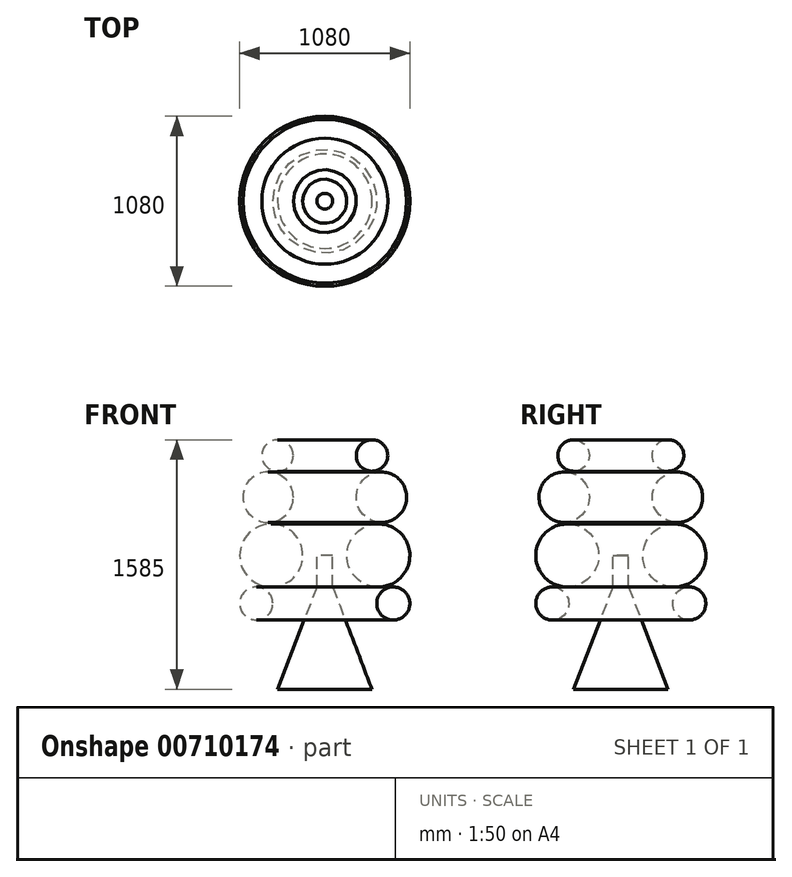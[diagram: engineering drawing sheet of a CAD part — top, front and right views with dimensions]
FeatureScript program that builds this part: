
annotation { "Feature Type Name" : "Feature", "Feature Type Description" : "" }
export const myFeature = defineFeature(function(context is Context, id is Id, definition is map)
    precondition{}
    {
        {
            var Q0;
            Q0=qCreatedBy(makeId("Front.planeOp"),FACE);
            var sketch = newSketch(context, id + "F0", { "sketchPlane" : qUnion([Q0])});
            skCircle(sketch, "E0", {"center": v(-340, 0) * mm, "radius": 200 * mm});
            skLineSegment(sketch, "E1", {"start": v(-340, 0) * mm, "end": v(0, 0) * mm});
            skLineSegment(sketch, "E2", {"start": v(0, 0) * mm, "end": v(0, 197.46) * mm});
            skSolve(sketch);
        }
        {
            var Q0;
            Q0=makeQuery(id+"F0.imprint","IMPRINT",FACE,{"disambiguationData":[TD([[makeQuery(id+"F0.imprint","IMPRINT",EDGE,{"derivedFrom":sQuery(id+"F0.wireOp",EDGE,"E0")}),1.0]])]});
            var Q1;
            Q1=sQuery(id+"F0.wireOp",EDGE,"E2");
            revolve(context, id + "F1", {"surfaceOperationType" : NewSurfaceOperationType.NEW, "entities" : qUnion([Q0]), "axis" : qUnion([Q1]), "revolveType" : RevolveType.FULL});
        }
        {
            var Q0;
            Q0=qCreatedBy(makeId("Front.planeOp"),FACE);
            var sketch = newSketch(context, id + "F2", { "sketchPlane" : qUnion([Q0])});
            skCircle(sketch, "E3", {"center": v(-435, -305) * mm, "radius": 105 * mm});
            skSolve(sketch);
        }
        {
            var Q0;
            Q0=makeQuery(id+"F2.imprint","IMPRINT",FACE,{"disambiguationData":[TD([[makeQuery(id+"F2.imprint","IMPRINT",EDGE,{"derivedFrom":sQuery(id+"F2.wireOp",EDGE,"E3")}),1.0]])]});
            var Q1;
            Q1=sQuery(id+"F0.wireOp",EDGE,"E2");
            revolve(context, id + "F3", {"surfaceOperationType" : NewSurfaceOperationType.NEW, "entities" : qUnion([Q0]), "axis" : qUnion([Q1]), "revolveType" : RevolveType.FULL});
        }
        {
            var Q0;
            Q0=qCreatedBy(makeId("Front.planeOp"),FACE);
            var sketch = newSketch(context, id + "F4", { "sketchPlane" : qUnion([Q0])});
            skCircle(sketch, "E4", {"center": v(-360, 370) * mm, "radius": 160 * mm});
            skSolve(sketch);
        }
        {
            var Q0;
            Q0=makeQuery(id+"F4.imprint","IMPRINT",FACE,{"disambiguationData":[TD([[makeQuery(id+"F4.imprint","IMPRINT",EDGE,{"derivedFrom":sQuery(id+"F4.wireOp",EDGE,"E4")}),1.0]])]});
            var Q1;
            Q1=sQuery(id+"F0.wireOp",EDGE,"E2");
            revolve(context, id + "F5", {"surfaceOperationType" : NewSurfaceOperationType.NEW, "entities" : qUnion([Q0]), "axis" : qUnion([Q1]), "revolveType" : RevolveType.FULL});
        }
        {
            var Q0;
            Q0=qCreatedBy(makeId("Front.planeOp"),FACE);
            var sketch = newSketch(context, id + "F6", { "sketchPlane" : qUnion([Q0])});
            skCircle(sketch, "E5", {"center": v(-300, 635) * mm, "radius": 100 * mm});
            skSolve(sketch);
        }
        {
            var Q0;
            Q0=makeQuery(id+"F6.imprint","IMPRINT",FACE,{"disambiguationData":[TD([[makeQuery(id+"F6.imprint","IMPRINT",EDGE,{"derivedFrom":sQuery(id+"F6.wireOp",EDGE,"E5")}),1.0]])]});
            var Q1;
            Q1=sQuery(id+"F0.wireOp",EDGE,"E2");
            revolve(context, id + "F7", {"surfaceOperationType" : NewSurfaceOperationType.NEW, "entities" : qUnion([Q0]), "axis" : qUnion([Q1]), "revolveType" : RevolveType.FULL});
        }
        {
            var Q0;
            Q0=qCreatedBy(makeId("Front.planeOp"),FACE);
            var sketch = newSketch(context, id + "F8", { "sketchPlane" : qUnion([Q0])});
            skLineSegment(sketch, "E6", {"start": v(0, 0) * mm, "end": v(0, -850) * mm});
            skLineSegment(sketch, "E7", {"start": v(-300, -850) * mm, "end": v(0, -850) * mm});
            skLineSegment(sketch, "E8", {"start": v(-300, -850) * mm, "end": v(-50, -200) * mm});
            skLineSegment(sketch, "E9", {"start": v(-50, 0) * mm, "end": v(-50, -200) * mm});
            skLineSegment(sketch, "E10", {"start": v(-50, 0) * mm, "end": v(0, 0) * mm});
            skSolve(sketch);
        }
        {
            var Q0;
            Q0=makeQuery(id+"F8.imprint","IMPRINT",FACE,{"disambiguationData":[TD([[makeQuery(id+"F8.imprint","IMPRINT",EDGE,{"derivedFrom":sQuery(id+"F8.wireOp",EDGE,"E6")}),-1.0]])]});
            var Q1;
            Q1=sQuery(id+"F8.wireOp",EDGE,"E6");
            revolve(context, id + "F9", {"surfaceOperationType" : NewSurfaceOperationType.NEW, "entities" : qUnion([Q0]), "axis" : qUnion([Q1]), "revolveType" : RevolveType.FULL});
        }
    });
